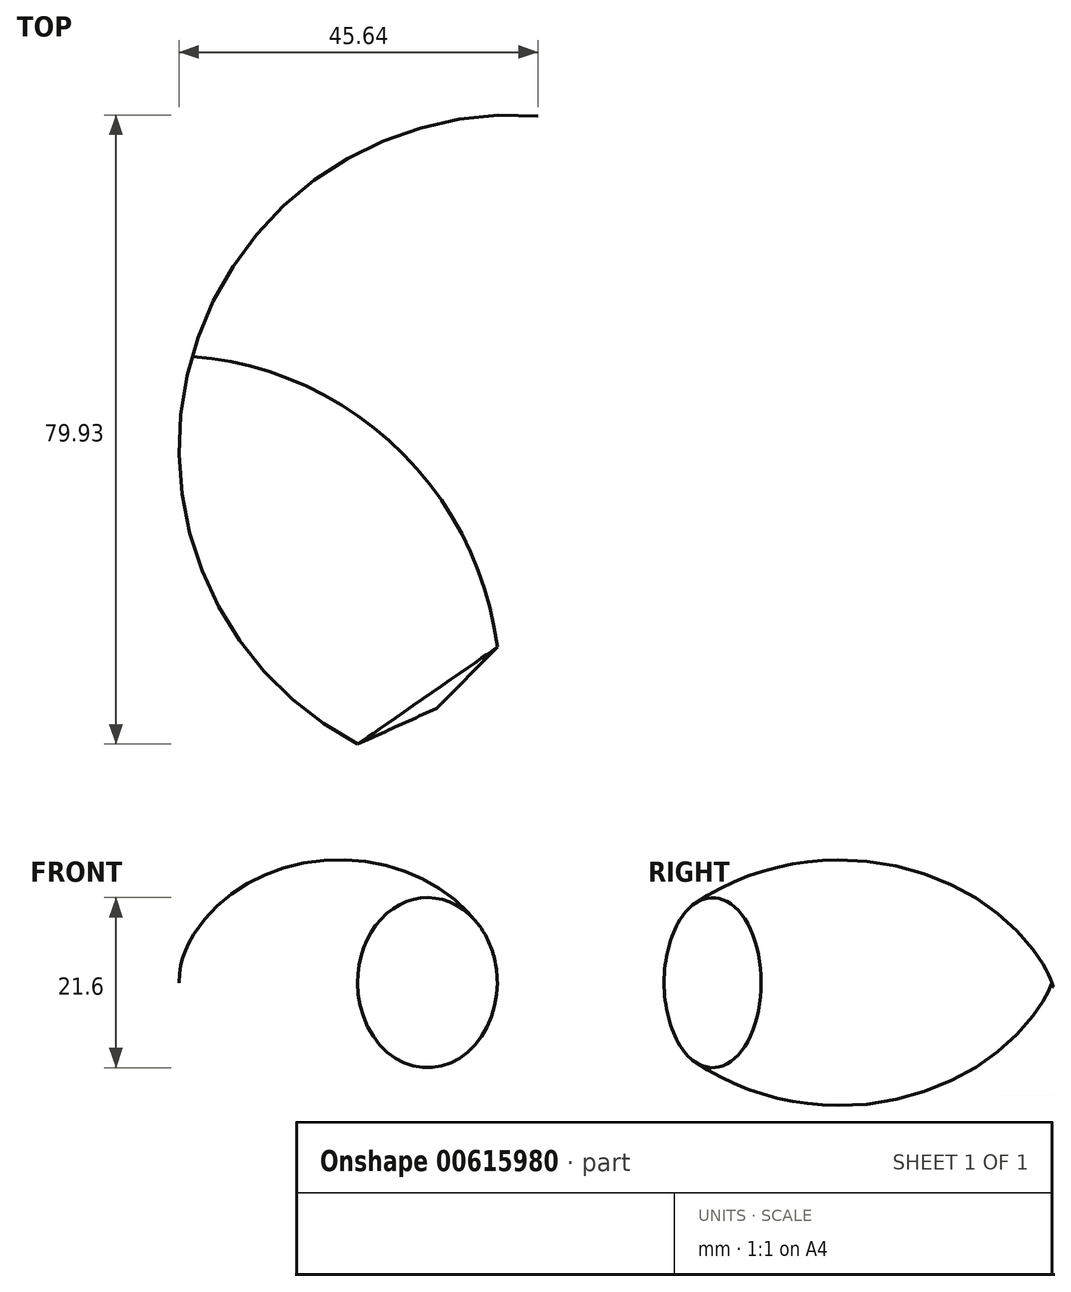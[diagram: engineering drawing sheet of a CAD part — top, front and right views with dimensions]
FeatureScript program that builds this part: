
annotation { "Feature Type Name" : "Feature", "Feature Type Description" : "" }
export const myFeature = defineFeature(function(context is Context, id is Id, definition is map)
    precondition{}
    {
        {
            var Q0;
            Q0=qCreatedBy(makeId("Top.planeOp"),FACE);
            var sketch = newSketch(context, id + "F0", { "sketchPlane" : qUnion([Q0])});
            skArc(sketch, "E0", {"start": v(-21.06, 49.26) * mm, "mid": v(-19.3, 20.88) * mm, "end": v(0, 0) * mm});
            skLineSegment(sketch, "E1", {"start": v(0, 0) * mm, "end": v(10, 4.53) * mm});
            skLineSegment(sketch, "E2", {"start": v(10, 4.53) * mm, "end": v(-21.06, 49.26) * mm});
            skSolve(sketch);
        }
        {
            var Q0;
            Q0=makeQuery(id+"F0.imprint","IMPRINT",FACE,{"disambiguationData":[TD([[makeQuery(id+"F0.imprint","IMPRINT",EDGE,{"derivedFrom":sQuery(id+"F0.wireOp",EDGE,"E0")}),1.0]])]});
            var Q1;
            Q1=sQuery(id+"F0.wireOp",EDGE,"E2");
            revolve(context, id + "F1", {"entities" : qUnion([Q0]), "axis" : qUnion([Q1]), "revolveType" : RevolveType.FULL});
        }
    });
